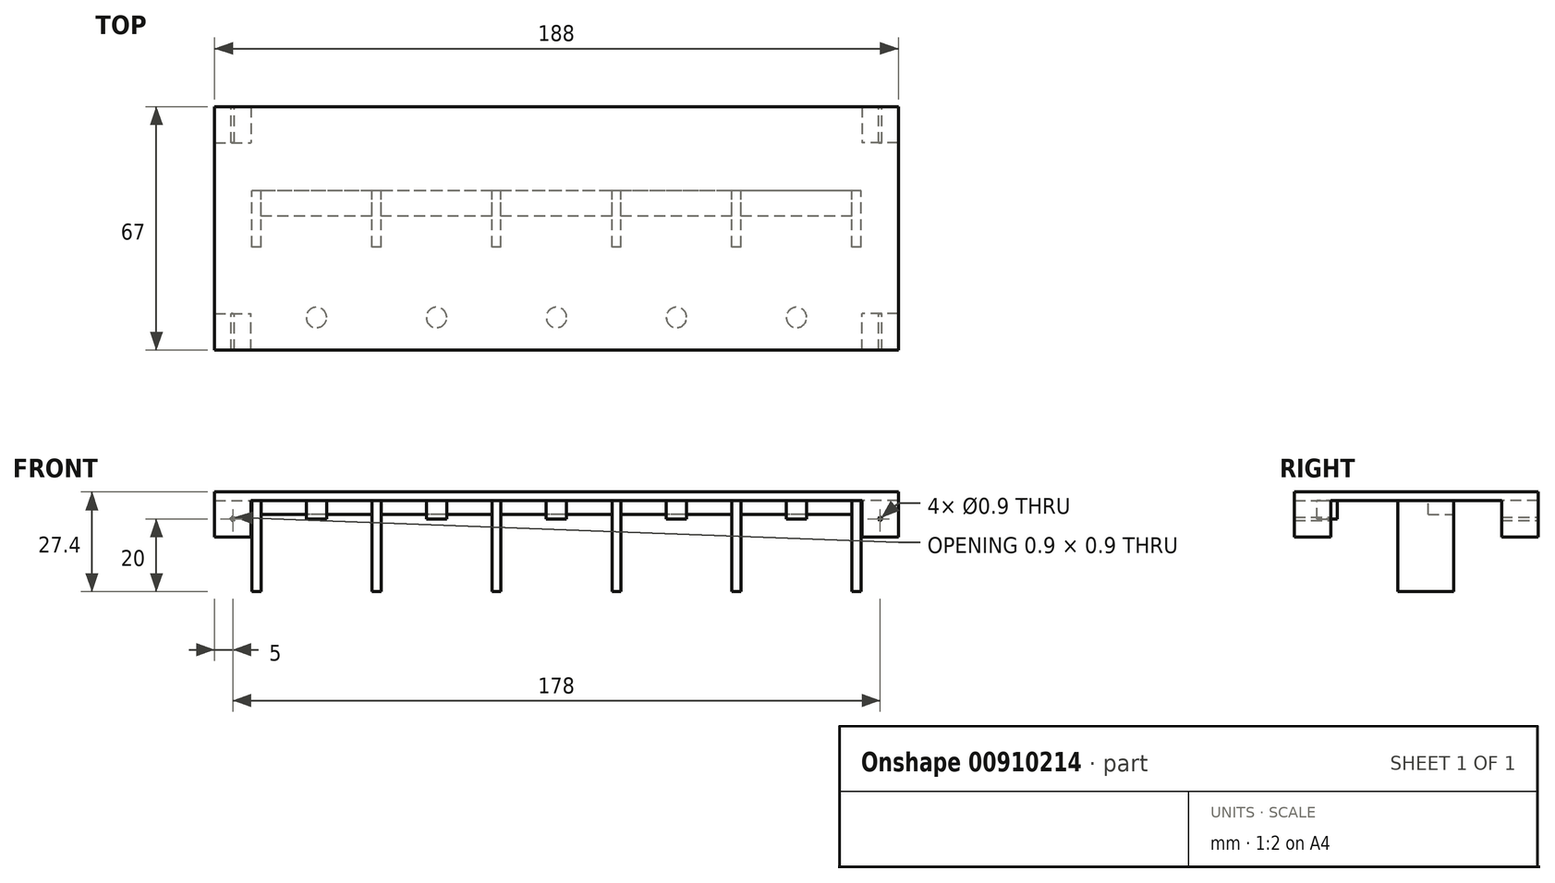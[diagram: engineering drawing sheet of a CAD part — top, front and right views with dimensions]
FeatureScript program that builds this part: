
annotation { "Feature Type Name" : "Feature", "Feature Type Description" : "" }
export const myFeature = defineFeature(function(context is Context, id is Id, definition is map)
    precondition{}
    {
        {
            var Q0;
            Q0=qCreatedBy(makeId("Top.planeOp"),FACE);
            var sketch = newSketch(context, id + "F0", { "sketchPlane" : qUnion([Q0])});
            skLineSegment(sketch, "E0.bottom", {"start": v(-94, 33.5) * mm, "end": v(94, 33.5) * mm});
            skLineSegment(sketch, "E0.top", {"start": v(-94, -33.5) * mm, "end": v(94, -33.5) * mm});
            skLineSegment(sketch, "E0.left", {"start": v(-94, 33.5) * mm, "end": v(-94, -33.5) * mm});
            skLineSegment(sketch, "E0.right", {"start": v(94, 33.5) * mm, "end": v(94, -33.5) * mm});
            skPoint(sketch, "E0.middle", {"position": v(0, 0) * mm});
            skSolve(sketch);
        }
        {
            var Q0;
            Q0 = qSketchRegion(id + "F0", true);
            extrude(context, id + "F1", {"entities" : qUnion([Q0]), "depth" : 2.4 * mm, "offsetDistance" : 25 * mm});
        }
        {
            var Q0;
            Q0=makeQuery(id+"F1.opExtrude","CAP_FACE",FACE,{"disambiguationData":[OSD([sQuery(id+"F0.wireOp",EDGE,"E0.bottom"),sQuery(id+"F0.wireOp",EDGE,"E0.top"),sQuery(id+"F0.wireOp",EDGE,"E0.left"),sQuery(id+"F0.wireOp",EDGE,"E0.right")])],"isStart":true});
            var sketch = newSketch(context, id + "F2", { "sketchPlane" : qUnion([Q0])});
            skLineSegment(sketch, "E1", {"start": v(94, 24.5) * mm, "end": v(-94, 24.5) * mm, "construction": true});
            skPoint(sketch, "E2", {"position": v(0, 24.5) * mm});
            skCircle(sketch, "E3", {"center": v(0, 24.5) * mm, "radius": 2.8 * mm});
            skCircle(sketch, "E4.1.0.0", {"center": v(33, 24.5) * mm, "radius": 2.8 * mm});
            skCircle(sketch, "E4.2.0.0", {"center": v(66, 24.5) * mm, "radius": 2.8 * mm});
            skLineSegment(sketch, "E4.direction1", {"start": v(0, 24.5) * mm, "end": v(33, 24.5) * mm, "construction": true});
            skCircle(sketch, "E5.1.0.0", {"center": v(-33, 24.5) * mm, "radius": 2.8 * mm});
            skCircle(sketch, "E5.2.0.0", {"center": v(-66, 24.5) * mm, "radius": 2.8 * mm});
            skLineSegment(sketch, "E5.direction1", {"start": v(0, 24.5) * mm, "end": v(-33, 24.5) * mm, "construction": true});
            skLineSegment(sketch, "E6.bottom", {"start": v(94, -33.5) * mm, "end": v(84, -33.5) * mm});
            skLineSegment(sketch, "E6.top", {"start": v(94, -23.5) * mm, "end": v(84, -23.5) * mm});
            skLineSegment(sketch, "E6.left", {"start": v(94, -33.5) * mm, "end": v(94, -23.5) * mm});
            skLineSegment(sketch, "E6.right", {"start": v(84, -33.5) * mm, "end": v(84, -23.5) * mm});
            skLineSegment(sketch, "E7.bottom", {"start": v(-94, -33.5) * mm, "end": v(-84, -33.5) * mm});
            skLineSegment(sketch, "E7.top", {"start": v(-94, -23.5) * mm, "end": v(-84, -23.5) * mm});
            skLineSegment(sketch, "E7.left", {"start": v(-94, -33.5) * mm, "end": v(-94, -23.5) * mm});
            skLineSegment(sketch, "E7.right", {"start": v(-84, -33.5) * mm, "end": v(-84, -23.5) * mm});
            skLineSegment(sketch, "E8.bottom", {"start": v(-94, 33.5) * mm, "end": v(-84, 33.5) * mm});
            skLineSegment(sketch, "E8.top", {"start": v(-94, 23.5) * mm, "end": v(-84, 23.5) * mm});
            skLineSegment(sketch, "E8.left", {"start": v(-94, 33.5) * mm, "end": v(-94, 23.5) * mm});
            skLineSegment(sketch, "E8.right", {"start": v(-84, 33.5) * mm, "end": v(-84, 23.5) * mm});
            skLineSegment(sketch, "E9.bottom", {"start": v(94, 33.5) * mm, "end": v(84, 33.5) * mm});
            skLineSegment(sketch, "E9.top", {"start": v(94, 23.5) * mm, "end": v(84, 23.5) * mm});
            skLineSegment(sketch, "E9.left", {"start": v(94, 33.5) * mm, "end": v(94, 23.5) * mm});
            skLineSegment(sketch, "E9.right", {"start": v(84, 33.5) * mm, "end": v(84, 23.5) * mm});
            skLineSegment(sketch, "E10", {"start": v(94, -6.8) * mm, "end": v(-94, -6.8) * mm, "construction": true});
            skLineSegment(sketch, "E11.bottom", {"start": v(84, -10.3) * mm, "end": v(-84, -10.3) * mm});
            skLineSegment(sketch, "E11.top", {"start": v(84, -3.3) * mm, "end": v(-84, -3.3) * mm});
            skLineSegment(sketch, "E11.left", {"start": v(84, -10.3) * mm, "end": v(84, -3.3) * mm});
            skLineSegment(sketch, "E11.right", {"start": v(-84, -10.3) * mm, "end": v(-84, -3.3) * mm});
            skPoint(sketch, "E11.middle", {"position": v(0, -6.8) * mm});
            skLineSegment(sketch, "E12.bottom", {"start": v(-15.25, 5.1) * mm, "end": v(-17.75, 5.1) * mm});
            skLineSegment(sketch, "E12.top", {"start": v(-15.25, -18.7) * mm, "end": v(-17.75, -18.7) * mm});
            skLineSegment(sketch, "E12.left", {"start": v(-15.25, 5.1) * mm, "end": v(-15.25, -18.7) * mm});
            skLineSegment(sketch, "E12.right", {"start": v(-17.75, 5.1) * mm, "end": v(-17.75, -18.7) * mm});
            skPoint(sketch, "E12.middle", {"position": v(-16.5, -6.8) * mm});
            skLineSegment(sketch, "E13.1.0.0", {"start": v(17.75, 5.1) * mm, "end": v(17.75, -18.7) * mm});
            skLineSegment(sketch, "E13.1.0.1", {"start": v(15.25, 5.1) * mm, "end": v(15.25, -18.7) * mm});
            skLineSegment(sketch, "E13.1.0.2", {"start": v(17.75, 5.1) * mm, "end": v(15.25, 5.1) * mm});
            skLineSegment(sketch, "E13.1.0.3", {"start": v(17.75, -18.7) * mm, "end": v(15.25, -18.7) * mm});
            skLineSegment(sketch, "E13.2.0.0", {"start": v(50.75, 5.1) * mm, "end": v(50.75, -18.7) * mm});
            skLineSegment(sketch, "E13.2.0.1", {"start": v(48.25, 5.1) * mm, "end": v(48.25, -18.7) * mm});
            skLineSegment(sketch, "E13.2.0.2", {"start": v(50.75, 5.1) * mm, "end": v(48.25, 5.1) * mm});
            skLineSegment(sketch, "E13.2.0.3", {"start": v(50.75, -18.7) * mm, "end": v(48.25, -18.7) * mm});
            skLineSegment(sketch, "E13.3.0.0", {"start": v(83.75, 5.1) * mm, "end": v(83.75, -18.7) * mm});
            skLineSegment(sketch, "E13.3.0.1", {"start": v(81.25, 5.1) * mm, "end": v(81.25, -18.7) * mm});
            skLineSegment(sketch, "E13.3.0.2", {"start": v(83.75, 5.1) * mm, "end": v(81.25, 5.1) * mm});
            skLineSegment(sketch, "E13.3.0.3", {"start": v(83.75, -18.7) * mm, "end": v(81.25, -18.7) * mm});
            skLineSegment(sketch, "E13.direction1", {"start": v(-15.25, -18.7) * mm, "end": v(17.75, -18.7) * mm, "construction": true});
            skLineSegment(sketch, "E14.1.0.0", {"start": v(-48.25, 5.1) * mm, "end": v(-50.75, 5.1) * mm});
            skLineSegment(sketch, "E14.1.0.1", {"start": v(-50.75, 5.1) * mm, "end": v(-50.75, -18.7) * mm});
            skLineSegment(sketch, "E14.1.0.2", {"start": v(-48.25, 5.1) * mm, "end": v(-48.25, -18.7) * mm});
            skLineSegment(sketch, "E14.1.0.3", {"start": v(-48.25, -18.7) * mm, "end": v(-50.75, -18.7) * mm});
            skLineSegment(sketch, "E14.2.0.0", {"start": v(-81.25, 5.1) * mm, "end": v(-83.75, 5.1) * mm});
            skLineSegment(sketch, "E14.2.0.1", {"start": v(-83.75, 5.1) * mm, "end": v(-83.75, -18.7) * mm});
            skLineSegment(sketch, "E14.2.0.2", {"start": v(-81.25, 5.1) * mm, "end": v(-81.25, -18.7) * mm});
            skLineSegment(sketch, "E14.2.0.3", {"start": v(-81.25, -18.7) * mm, "end": v(-83.75, -18.7) * mm});
            skLineSegment(sketch, "E14.direction1", {"start": v(-17.75, 5.1) * mm, "end": v(-50.75, 5.1) * mm, "construction": true});
            skLineSegment(sketch, "E15", {"start": v(-82.54, -10.3) * mm, "end": v(-82.54, -3.3) * mm});
            skLineSegment(sketch, "E16", {"start": v(82.54, -3.3) * mm, "end": v(82.54, -10.3) * mm});
            skSolve(sketch);
        }
        {
            var Q0;
            Q0=makeQuery(id+"F2.imprint","IMPRINT",FACE,{"disambiguationData":[TD([[makeQuery(id+"F2.imprint","IMPRINT",EDGE,{"derivedFrom":sQuery(id+"F2.wireOp",EDGE,"E4.2.0.0")}),1.0]])]});
            var Q1;
            Q1=makeQuery(id+"F2.imprint","IMPRINT",FACE,{"disambiguationData":[TD([[makeQuery(id+"F2.imprint","IMPRINT",EDGE,{"derivedFrom":sQuery(id+"F2.wireOp",EDGE,"E4.1.0.0")}),1.0]])]});
            var Q2;
            Q2=makeQuery(id+"F2.imprint","IMPRINT",FACE,{"disambiguationData":[TD([[makeQuery(id+"F2.imprint","IMPRINT",EDGE,{"derivedFrom":sQuery(id+"F2.wireOp",EDGE,"E3")}),1.0]])]});
            var Q3;
            Q3=makeQuery(id+"F2.imprint","IMPRINT",FACE,{"disambiguationData":[TD([[makeQuery(id+"F2.imprint","IMPRINT",EDGE,{"derivedFrom":sQuery(id+"F2.wireOp",EDGE,"E5.1.0.0")}),1.0]])]});
            var Q4;
            Q4=makeQuery(id+"F2.imprint","IMPRINT",FACE,{"disambiguationData":[TD([[makeQuery(id+"F2.imprint","IMPRINT",EDGE,{"derivedFrom":sQuery(id+"F2.wireOp",EDGE,"E5.2.0.0")}),1.0]])]});
            extrude(context, id + "F3", {"entities" : qUnion([Q0, Q1, Q2, Q3, Q4]), "operationType" : NewBodyOperationType.ADD, "depth" : 5 * mm, "offsetDistance" : 25 * mm});
        }
        {
            var Q0;
            Q0=makeQuery(id+"F2.imprint","IMPRINT",FACE,{"disambiguationData":[TD([[makeQuery(id+"F2.imprint","IMPRINT",EDGE,{"derivedFrom":sQuery(id+"F2.wireOp",EDGE,"E6.bottom")}),1.0]])]});
            var Q1;
            Q1=makeQuery(id+"F2.imprint","IMPRINT",FACE,{"disambiguationData":[TD([[makeQuery(id+"F2.imprint","IMPRINT",EDGE,{"derivedFrom":sQuery(id+"F2.wireOp",EDGE,"E9.bottom")}),-1.0]])]});
            var Q2;
            Q2=makeQuery(id+"F2.imprint","IMPRINT",FACE,{"disambiguationData":[TD([[makeQuery(id+"F2.imprint","IMPRINT",EDGE,{"derivedFrom":sQuery(id+"F2.wireOp",EDGE,"E7.bottom")}),1.0]])]});
            var Q3;
            Q3=makeQuery(id+"F2.imprint","IMPRINT",FACE,{"disambiguationData":[TD([[makeQuery(id+"F2.imprint","IMPRINT",EDGE,{"derivedFrom":sQuery(id+"F2.wireOp",EDGE,"E8.bottom")}),-1.0]])]});
            extrude(context, id + "F4", {"entities" : qUnion([Q0, Q1, Q2, Q3]), "operationType" : NewBodyOperationType.ADD, "depth" : 10 * mm, "offsetDistance" : 25 * mm});
        }
        {
            var Q0;
            {var subQ0=sQuery(id+"F2.wireOp",EDGE,"E14.1.0.2");var subQ1=sQuery(id+"F2.wireOp",EDGE,"E11.bottom");var subQ2=makeQuery(id+"F2.imprint","INTERSECT",VERTEX,{"derivedFrom":[subQ1,subQ0]});Q0=makeQuery(id+"F2.imprint","IMPRINT",FACE,{"disambiguationData":[TD([[makeQuery(id+"F2.imprint","IMPRINT",EDGE,{"disambiguationData":[TD([[subQ2,-1.0]])],"derivedFrom":subQ1}),-1.0]])]});}
            var Q1;
            {var subQ0=sQuery(id+"F2.wireOp",EDGE,"E12.left");var subQ1=sQuery(id+"F2.wireOp",EDGE,"E11.bottom");var subQ2=makeQuery(id+"F2.imprint","INTERSECT",VERTEX,{"derivedFrom":[subQ1,subQ0]});Q1=makeQuery(id+"F2.imprint","IMPRINT",FACE,{"disambiguationData":[TD([[makeQuery(id+"F2.imprint","IMPRINT",EDGE,{"disambiguationData":[TD([[subQ2,-1.0]])],"derivedFrom":subQ1}),-1.0]])]});}
            var Q2;
            {var subQ0=sQuery(id+"F2.wireOp",EDGE,"E13.1.0.0");var subQ1=sQuery(id+"F2.wireOp",EDGE,"E11.bottom");var subQ2=makeQuery(id+"F2.imprint","INTERSECT",VERTEX,{"derivedFrom":[subQ1,subQ0]});Q2=makeQuery(id+"F2.imprint","IMPRINT",FACE,{"disambiguationData":[TD([[makeQuery(id+"F2.imprint","IMPRINT",EDGE,{"disambiguationData":[TD([[subQ2,-1.0]])],"derivedFrom":subQ1}),-1.0]])]});}
            var Q3;
            {var subQ0=sQuery(id+"F2.wireOp",EDGE,"E13.2.0.0");var subQ1=sQuery(id+"F2.wireOp",EDGE,"E11.bottom");var subQ2=makeQuery(id+"F2.imprint","INTERSECT",VERTEX,{"derivedFrom":[subQ1,subQ0]});Q3=makeQuery(id+"F2.imprint","IMPRINT",FACE,{"disambiguationData":[TD([[makeQuery(id+"F2.imprint","IMPRINT",EDGE,{"disambiguationData":[TD([[subQ2,-1.0]])],"derivedFrom":subQ1}),-1.0]])]});}
            var Q4;
            {var subQ0=sQuery(id+"F2.wireOp",EDGE,"E14.2.0.2");var subQ1=sQuery(id+"F2.wireOp",EDGE,"E11.bottom");var subQ2=makeQuery(id+"F2.imprint","INTERSECT",VERTEX,{"derivedFrom":[subQ1,subQ0]});Q4=makeQuery(id+"F2.imprint","IMPRINT",FACE,{"disambiguationData":[TD([[makeQuery(id+"F2.imprint","IMPRINT",EDGE,{"disambiguationData":[TD([[subQ2,-1.0]])],"derivedFrom":subQ1}),-1.0]])]});}
            var Q5;
            {var subQ0=sQuery(id+"F2.wireOp",EDGE,"E13.3.0.0");var subQ1=sQuery(id+"F2.wireOp",EDGE,"E11.bottom");var subQ2=makeQuery(id+"F2.imprint","INTERSECT",VERTEX,{"derivedFrom":[subQ1,subQ0]});Q5=makeQuery(id+"F2.imprint","IMPRINT",FACE,{"disambiguationData":[TD([[makeQuery(id+"F2.imprint","IMPRINT",EDGE,{"disambiguationData":[TD([[subQ2,-1.0]])],"derivedFrom":subQ1}),-1.0]])]});}
            var Q6;
            {var subQ5=sQuery(id+"F2.wireOp",EDGE,"E14.2.0.0");Q6=makeQuery(id+"F2.imprint","IMPRINT",FACE,{"disambiguationData":[TD([[makeQuery(id+"F2.imprint","IMPRINT",EDGE,{"derivedFrom":subQ5}),1.0]])]});}
            var Q7;
            {var subQ5=sQuery(id+"F2.wireOp",EDGE,"E14.1.0.0");Q7=makeQuery(id+"F2.imprint","IMPRINT",FACE,{"disambiguationData":[TD([[makeQuery(id+"F2.imprint","IMPRINT",EDGE,{"derivedFrom":subQ5}),1.0]])]});}
            var Q8;
            {var subQ5=sQuery(id+"F2.wireOp",EDGE,"E12.bottom");Q8=makeQuery(id+"F2.imprint","IMPRINT",FACE,{"disambiguationData":[TD([[makeQuery(id+"F2.imprint","IMPRINT",EDGE,{"derivedFrom":subQ5}),1.0]])]});}
            var Q9;
            {var subQ5=sQuery(id+"F2.wireOp",EDGE,"E13.1.0.2");Q9=makeQuery(id+"F2.imprint","IMPRINT",FACE,{"disambiguationData":[TD([[makeQuery(id+"F2.imprint","IMPRINT",EDGE,{"derivedFrom":subQ5}),1.0]])]});}
            var Q10;
            {var subQ5=sQuery(id+"F2.wireOp",EDGE,"E13.2.0.2");Q10=makeQuery(id+"F2.imprint","IMPRINT",FACE,{"disambiguationData":[TD([[makeQuery(id+"F2.imprint","IMPRINT",EDGE,{"derivedFrom":subQ5}),1.0]])]});}
            var Q11;
            {var subQ5=sQuery(id+"F2.wireOp",EDGE,"E13.3.0.2");Q11=makeQuery(id+"F2.imprint","IMPRINT",FACE,{"disambiguationData":[TD([[makeQuery(id+"F2.imprint","IMPRINT",EDGE,{"derivedFrom":subQ5}),1.0]])]});}
            var Q12;
            {var subQ0=sQuery(id+"F2.wireOp",EDGE,"E15");Q12=makeQuery(id+"F2.imprint","IMPRINT",FACE,{"disambiguationData":[TD([[makeQuery(id+"F2.imprint","IMPRINT",EDGE,{"derivedFrom":subQ0}),1.0]])]});}
            var Q13;
            {var subQ0=sQuery(id+"F2.wireOp",EDGE,"E16");Q13=makeQuery(id+"F2.imprint","IMPRINT",FACE,{"disambiguationData":[TD([[makeQuery(id+"F2.imprint","IMPRINT",EDGE,{"derivedFrom":subQ0}),-1.0]])]});}
            extrude(context, id + "F5", {"entities" : qUnion([Q0, Q1, Q2, Q3, Q4, Q5, Q6, Q7, Q8, Q9, Q10, Q11, Q12, Q13]), "operationType" : NewBodyOperationType.ADD, "depth" : 25 * mm, "offsetDistance" : 25 * mm});
        }
        {
            var Q0;
            {var subQ0=sQuery(id+"F2.wireOp",EDGE,"E13.3.0.1");var subQ1=sQuery(id+"F2.wireOp",EDGE,"E11.bottom");var subQ2=makeQuery(id+"F2.imprint","INTERSECT",VERTEX,{"derivedFrom":[subQ1,subQ0]});Q0=makeQuery(id+"F2.imprint","IMPRINT",FACE,{"disambiguationData":[TD([[makeQuery(id+"F2.imprint","IMPRINT",EDGE,{"disambiguationData":[TD([[subQ2,-1.0]])],"derivedFrom":subQ1}),-1.0]])]});}
            var Q1;
            {var subQ0=sQuery(id+"F2.wireOp",EDGE,"E13.2.0.1");var subQ1=sQuery(id+"F2.wireOp",EDGE,"E11.bottom");var subQ2=makeQuery(id+"F2.imprint","INTERSECT",VERTEX,{"derivedFrom":[subQ1,subQ0]});Q1=makeQuery(id+"F2.imprint","IMPRINT",FACE,{"disambiguationData":[TD([[makeQuery(id+"F2.imprint","IMPRINT",EDGE,{"disambiguationData":[TD([[subQ2,-1.0]])],"derivedFrom":subQ1}),-1.0]])]});}
            var Q2;
            {var subQ0=sQuery(id+"F2.wireOp",EDGE,"E13.1.0.1");var subQ1=sQuery(id+"F2.wireOp",EDGE,"E11.bottom");var subQ2=makeQuery(id+"F2.imprint","INTERSECT",VERTEX,{"derivedFrom":[subQ1,subQ0]});Q2=makeQuery(id+"F2.imprint","IMPRINT",FACE,{"disambiguationData":[TD([[makeQuery(id+"F2.imprint","IMPRINT",EDGE,{"disambiguationData":[TD([[subQ2,-1.0]])],"derivedFrom":subQ1}),-1.0]])]});}
            var Q3;
            {var subQ0=sQuery(id+"F2.wireOp",EDGE,"E12.right");var subQ1=sQuery(id+"F2.wireOp",EDGE,"E11.bottom");var subQ2=makeQuery(id+"F2.imprint","INTERSECT",VERTEX,{"derivedFrom":[subQ1,subQ0]});Q3=makeQuery(id+"F2.imprint","IMPRINT",FACE,{"disambiguationData":[TD([[makeQuery(id+"F2.imprint","IMPRINT",EDGE,{"disambiguationData":[TD([[subQ2,-1.0]])],"derivedFrom":subQ1}),-1.0]])]});}
            var Q4;
            {var subQ0=sQuery(id+"F2.wireOp",EDGE,"E14.1.0.1");var subQ1=sQuery(id+"F2.wireOp",EDGE,"E11.bottom");var subQ2=makeQuery(id+"F2.imprint","INTERSECT",VERTEX,{"derivedFrom":[subQ1,subQ0]});Q4=makeQuery(id+"F2.imprint","IMPRINT",FACE,{"disambiguationData":[TD([[makeQuery(id+"F2.imprint","IMPRINT",EDGE,{"disambiguationData":[TD([[subQ2,-1.0]])],"derivedFrom":subQ1}),-1.0]])]});}
            extrude(context, id + "F6", {"entities" : qUnion([Q0, Q1, Q2, Q3, Q4]), "operationType" : NewBodyOperationType.ADD, "depth" : 3.8 * mm, "offsetDistance" : 25 * mm});
        }
        {
            var Q0;
            Q0=makeQuery(id+"F4.boolean.opBoolean","MERGE",FACE,{"derivedFrom":[makeQuery(id+"F1.opExtrude","SWEPT_FACE",FACE,{"disambiguationData":[OSD([sQuery(id+"F0.wireOp",EDGE,"E0.bottom")])]}),makeQuery(id+"F4.opExtrude","SWEPT_FACE",FACE,{"disambiguationData":[OSD([sQuery(id+"F2.wireOp",EDGE,"E6.bottom")])]}),makeQuery(id+"F4.opExtrude","SWEPT_FACE",FACE,{"disambiguationData":[OSD([sQuery(id+"F2.wireOp",EDGE,"E7.bottom")])]})]});
            var sketch = newSketch(context, id + "F7", { "sketchPlane" : qUnion([Q0])});
            skCircle(sketch, "E17", {"center": v(89, -5) * mm, "radius": 0.45 * mm});
            skPoint(sketch, "E17.centerSnap0", {"position": v(89, -10) * mm});
            skPoint(sketch, "E17.centerSnap1", {"position": v(84, -5) * mm});
            skCircle(sketch, "E18", {"center": v(-89, -5) * mm, "radius": 0.45 * mm});
            skPoint(sketch, "E18.centerSnap0", {"position": v(-89, -10) * mm});
            skPoint(sketch, "E18.centerSnap1", {"position": v(-84, -5) * mm});
            skSolve(sketch);
        }
        {
            var Q0;
            Q0 = qSketchRegion(id + "F7", true);
            extrude(context, id + "F8", {"entities" : qUnion([Q0]), "operationType" : NewBodyOperationType.REMOVE, "endBound" : BoundingType.THROUGH_ALL, "oppositeDirection" : true, "depth" : 25 * mm, "offsetDistance" : 25 * mm});
        }
    });
